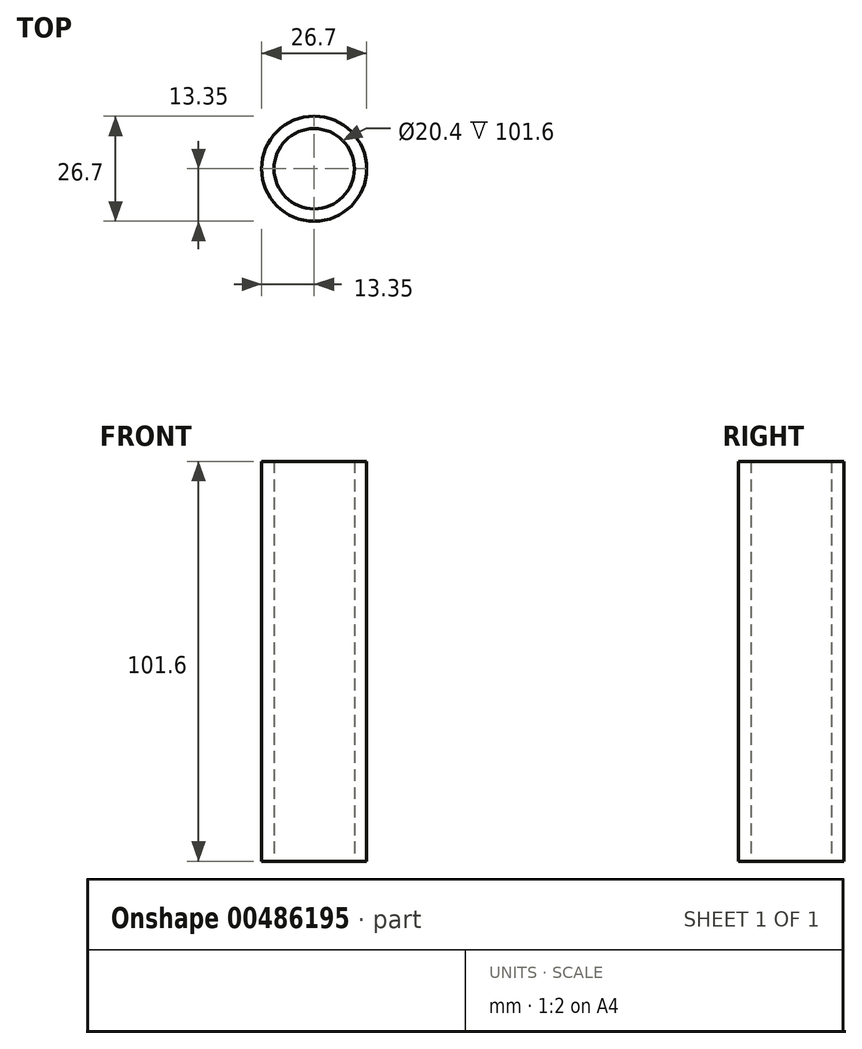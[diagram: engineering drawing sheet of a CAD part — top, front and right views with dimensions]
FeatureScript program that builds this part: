
annotation { "Feature Type Name" : "Feature", "Feature Type Description" : "" }
export const myFeature = defineFeature(function(context is Context, id is Id, definition is map)
    precondition{}
    {
        {
            var Q0;
            Q0=qCreatedBy(makeId("Top.planeOp"),FACE);
            var sketch = newSketch(context, id + "F0", { "sketchPlane" : qUnion([Q0])});
            skCircle(sketch, "E0", {"center": v(0, 0) * mm, "radius": 13.35 * mm});
            skCircle(sketch, "E1", {"center": v(0, 0) * mm, "radius": 10.2 * mm});
            skSolve(sketch);
        }
        {
            var Q0;
            Q0=makeQuery(id+"F0.imprint","IMPRINT",FACE,{"disambiguationData":[TD([[makeQuery(id+"F0.imprint","IMPRINT",EDGE,{"derivedFrom":sQuery(id+"F0.wireOp",EDGE,"E0")}),1.0]])]});
            extrude(context, id + "F1", {"entities" : qUnion([Q0]), "depth" : 101.6 * mm});
        }
    });
